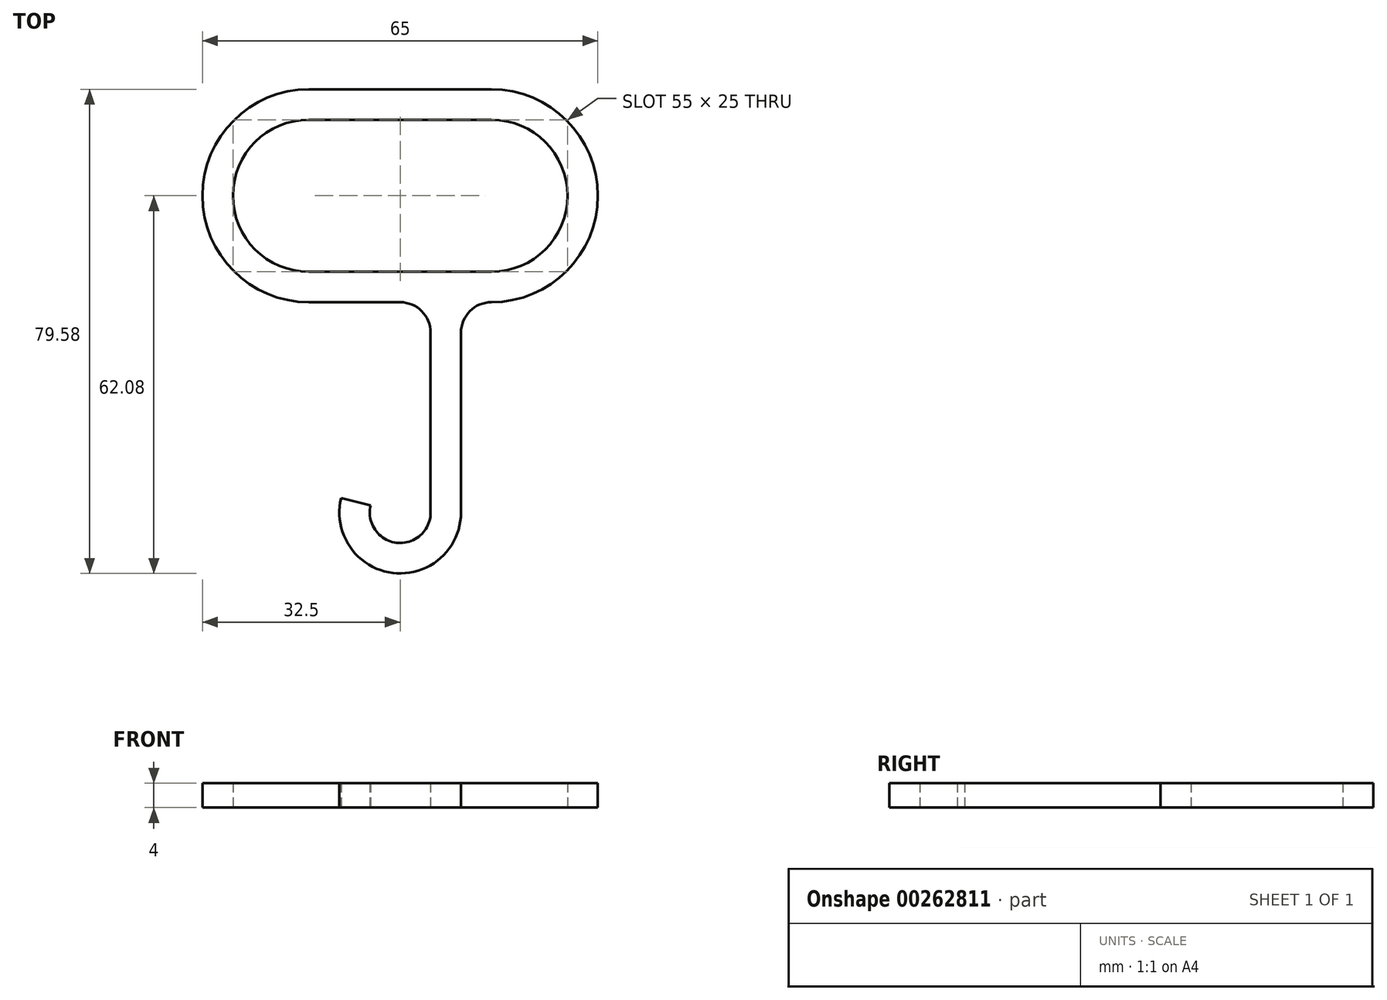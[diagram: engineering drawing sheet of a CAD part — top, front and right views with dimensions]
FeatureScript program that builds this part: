
annotation { "Feature Type Name" : "Feature", "Feature Type Description" : "" }
export const myFeature = defineFeature(function(context is Context, id is Id, definition is map)
    precondition{}
    {
        {
            var Q0;
            Q0=qCreatedBy(makeId("Top.planeOp"),FACE);
            var sketch = newSketch(context, id + "F0", { "sketchPlane" : qUnion([Q0])});
            skArc(sketch, "E0", {"start": v(-15, 12.5) * mm, "mid": v(-27.5, 0) * mm, "end": v(-15, -12.5) * mm});
            skLineSegment(sketch, "E1", {"start": v(-15, 0) * mm, "end": v(0, 0) * mm, "construction": true});
            skLineSegment(sketch, "E2", {"start": v(-15, 12.5) * mm, "end": v(0, 12.5) * mm});
            skLineSegment(sketch, "E3", {"start": v(-15, -12.5) * mm, "end": v(0, -12.5) * mm});
            skArc(sketch, "E4", {"start": v(-4.85, -50.87) * mm, "mid": v(-0.6, -57.04) * mm, "end": v(5, -52.08) * mm});
            skArc(sketch, "E5", {"start": v(-9.7, -49.67) * mm, "mid": v(-1.21, -62) * mm, "end": v(10, -52.08) * mm});
            skLineSegment(sketch, "E6", {"start": v(0, -41.38) * mm, "end": v(10, -41.38) * mm, "construction": true});
            skLineSegment(sketch, "E7", {"start": v(10, -52.08) * mm, "end": v(10, -20.86) * mm});
            skLineSegment(sketch, "E8", {"start": v(5, -43.42) * mm, "end": v(5, -18.8) * mm});
            skLineSegment(sketch, "E9", {"start": v(0, 12.5) * mm, "end": v(0, -22.64) * mm, "construction": true});
            skLineSegment(sketch, "E10.0", {"start": v(-15, 17.5) * mm, "end": v(0, 17.5) * mm});
            skArc(sketch, "E10.1", {"start": v(-15, 17.5) * mm, "mid": v(-32.5, 0) * mm, "end": v(-15, -17.5) * mm});
            skLineSegment(sketch, "E10.2", {"start": v(-15, -17.5) * mm, "end": v(0, -17.5) * mm});
            skLineSegment(sketch, "E11.MirrorCS", {"start": v(15, 12.5) * mm, "end": v(0, 12.5) * mm});
            skLineSegment(sketch, "E12.MirrorCS", {"start": v(15, 17.5) * mm, "end": v(0, 17.5) * mm});
            skArc(sketch, "E13.MirrorCS", {"start": v(15, 17.5) * mm, "mid": v(32.5, 0) * mm, "end": v(15, -17.5) * mm});
            skArc(sketch, "E14.MirrorCS", {"start": v(15, 12.5) * mm, "mid": v(27.5, 0) * mm, "end": v(15, -12.5) * mm});
            skLineSegment(sketch, "E15.MirrorCS", {"start": v(15, -12.5) * mm, "end": v(0, -12.5) * mm});
            skLineSegment(sketch, "E16.MirrorCS", {"start": v(15, -17.5) * mm, "end": v(10, -17.5) * mm});
            skLineSegment(sketch, "E17", {"start": v(5, -18.8) * mm, "end": v(5, -17.5) * mm});
            skLineSegment(sketch, "E18", {"start": v(10, -20.86) * mm, "end": v(10, -17.5) * mm});
            skPoint(sketch, "E19.orphan", {"position": v(10, -15.84) * mm});
            skLineSegment(sketch, "E20.trimOffspring", {"start": v(5, -17.5) * mm, "end": v(0, -17.5) * mm});
            skLineSegment(sketch, "E21", {"start": v(5, -43.42) * mm, "end": v(5, -52.08) * mm});
            skLineSegment(sketch, "E22", {"start": v(-4.85, -50.87) * mm, "end": v(-9.7, -49.67) * mm});
            skSolve(sketch);
        }
        {
            var Q0;
            Q0=makeQuery(id+"F0.imprint","IMPRINT",FACE,{"disambiguationData":[TD([[makeQuery(id+"F0.imprint","IMPRINT",EDGE,{"derivedFrom":sQuery(id+"F0.wireOp",EDGE,"E0")}),-1.0]])]});
            extrude(context, id + "F1", {"entities" : qUnion([Q0]), "depth" : 4 * mm});
        }
        {
            var Q0;
            Q0=makeQuery(id+"F1.opExtrude","SWEPT_EDGE",EDGE,{"disambiguationData":[OSD([sQuery(id+"F0.wireOp",EDGE,"E17"),sQuery(id+"F0.wireOp",EDGE,"E20.trimOffspring")])]});
            var Q1;
            Q1=makeQuery(id+"F1.opExtrude","SWEPT_EDGE",EDGE,{"disambiguationData":[OSD([sQuery(id+"F0.wireOp",EDGE,"E16.MirrorCS"),sQuery(id+"F0.wireOp",EDGE,"E18")])]});
            fillet(context, id + "F2", {"entities" : qUnion([Q0, Q1]), "radius" : 5 * mm, "tangentPropagation" : true, "allowEdgeOverflow" : false});
        }
    });
